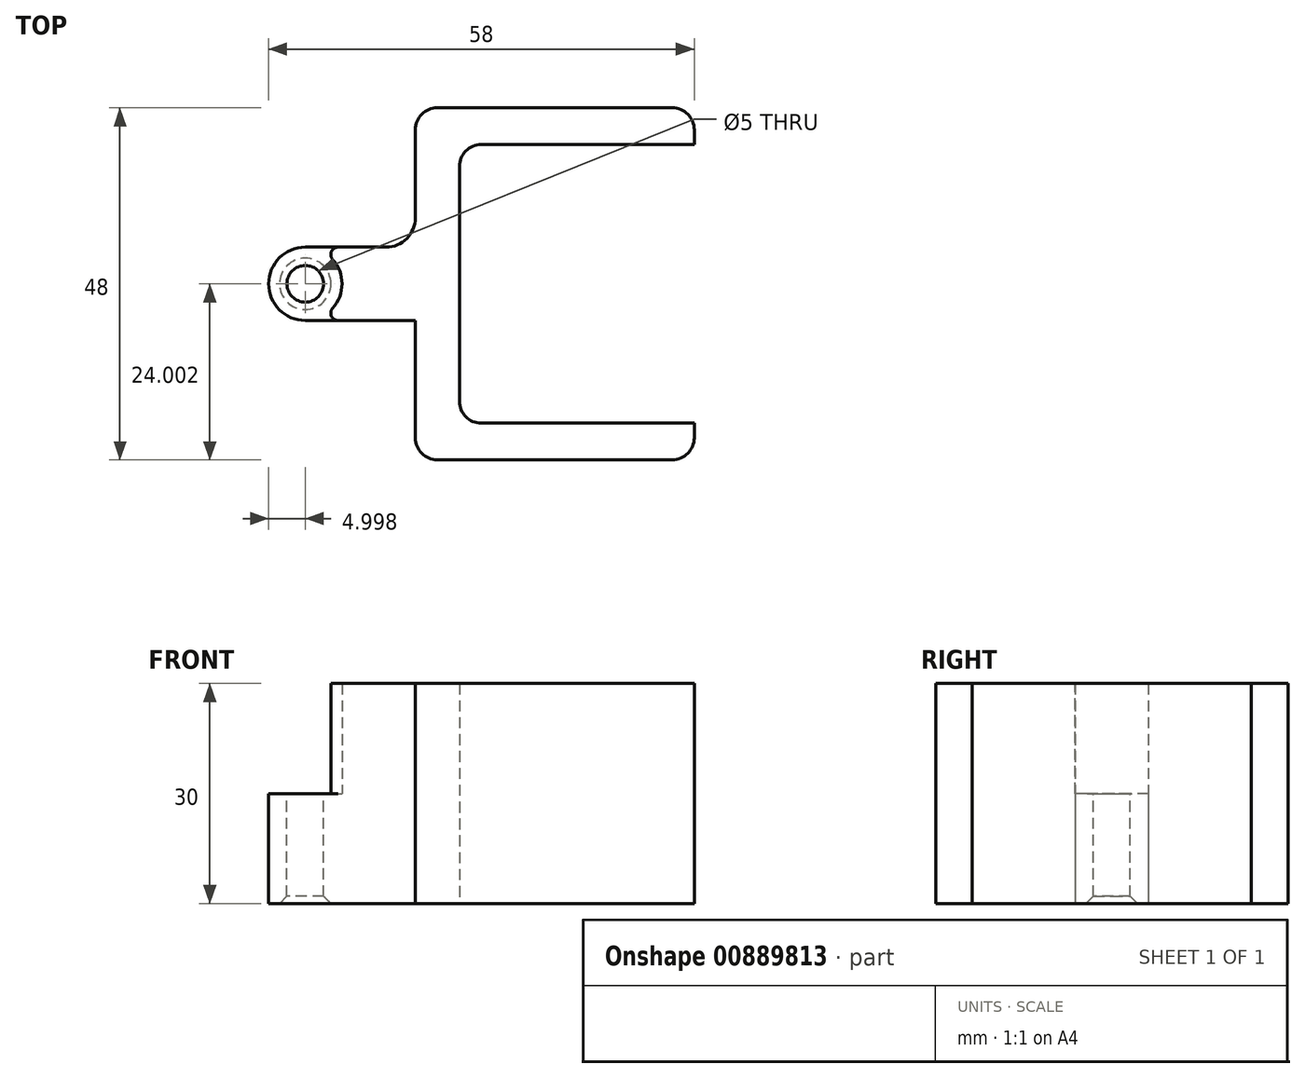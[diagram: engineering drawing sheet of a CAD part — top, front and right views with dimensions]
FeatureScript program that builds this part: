
annotation { "Feature Type Name" : "Feature", "Feature Type Description" : "" }
export const myFeature = defineFeature(function(context is Context, id is Id, definition is map)
    precondition{}
    {
        {
            var Q0;
            Q0=qCreatedBy(makeId("Top.planeOp"),FACE);
            var sketch = newSketch(context, id + "F0", { "sketchPlane" : qUnion([Q0])});
            skCircle(sketch, "E0", {"center": v(-71.58, 14.1) * mm, "radius": 5 * mm});
            skLineSegment(sketch, "E1.bottom", {"start": v(-71.58, 19.1) * mm, "end": v(-56.58, 19.1) * mm});
            skLineSegment(sketch, "E1.top", {"start": v(-71.58, 9.1) * mm, "end": v(-56.58, 9.1) * mm});
            skLineSegment(sketch, "E1.left", {"start": v(-71.58, 19.1) * mm, "end": v(-71.58, 9.1) * mm});
            skLineSegment(sketch, "E1.right", {"start": v(-56.58, 19.1) * mm, "end": v(-56.58, 9.1) * mm});
            skLineSegment(sketch, "E2.bottom", {"start": v(-56.58, 33.1) * mm, "end": v(-50.58, 33.1) * mm});
            skLineSegment(sketch, "E2.top", {"start": v(-56.58, -4.9) * mm, "end": v(-50.58, -4.9) * mm});
            skLineSegment(sketch, "E2.left", {"start": v(-56.58, 33.1) * mm, "end": v(-56.58, -4.9) * mm});
            skLineSegment(sketch, "E2.right", {"start": v(-50.58, 33.1) * mm, "end": v(-50.58, -4.9) * mm});
            skLineSegment(sketch, "E3.bottom", {"start": v(-56.58, 33.1) * mm, "end": v(-18.58, 33.1) * mm});
            skLineSegment(sketch, "E3.top", {"start": v(-56.58, 38.1) * mm, "end": v(-18.58, 38.1) * mm});
            skLineSegment(sketch, "E3.left", {"start": v(-56.58, 33.1) * mm, "end": v(-56.58, 38.1) * mm});
            skLineSegment(sketch, "E3.right", {"start": v(-18.58, 33.1) * mm, "end": v(-18.58, 38.1) * mm});
            skLineSegment(sketch, "E4.bottom", {"start": v(-56.58, -4.9) * mm, "end": v(-18.58, -4.9) * mm});
            skLineSegment(sketch, "E4.top", {"start": v(-56.58, -9.9) * mm, "end": v(-18.58, -9.9) * mm});
            skLineSegment(sketch, "E4.left", {"start": v(-56.58, -4.9) * mm, "end": v(-56.58, -9.9) * mm});
            skLineSegment(sketch, "E4.right", {"start": v(-18.58, -4.9) * mm, "end": v(-18.58, -9.9) * mm});
            skSolve(sketch);
        }
        {
            var Q0;
            {var subQ1=sQuery(id+"F0.wireOp",EDGE,"E1.bottom");Q0=makeQuery(id+"F0.imprint","IMPRINT",FACE,{"disambiguationData":[TD([[makeQuery(id+"F0.imprint","IMPRINT",EDGE,{"derivedFrom":subQ1}),-1.0]])]});}
            extrude(context, id + "F1", {"entities" : qUnion([Q0]), "depth" : 30 * mm, "offsetDistance" : 25 * mm});
        }
        {
            var Q0;
            Q0=makeQuery(id+"F0.imprint","IMPRINT",FACE,{"disambiguationData":[TD([[makeQuery(id+"F0.imprint","IMPRINT",EDGE,{"derivedFrom":sQuery(id+"F0.wireOp",EDGE,"E3.top")}),-1.0]])]});
            var Q1;
            {var subQ0=sQuery(id+"F0.wireOp",EDGE,"E2.right");Q1=makeQuery(id+"F0.imprint","IMPRINT",FACE,{"disambiguationData":[TD([[makeQuery(id+"F0.imprint","IMPRINT",EDGE,{"derivedFrom":subQ0}),-1.0]])]});}
            var Q2;
            Q2=makeQuery(id+"F0.imprint","IMPRINT",FACE,{"disambiguationData":[TD([[makeQuery(id+"F0.imprint","IMPRINT",EDGE,{"derivedFrom":sQuery(id+"F0.wireOp",EDGE,"E4.top")}),1.0]])]});
            extrude(context, id + "F2", {"entities" : qUnion([Q0, Q1, Q2]), "operationType" : NewBodyOperationType.ADD, "depth" : 30 * mm, "offsetDistance" : 25 * mm});
        }
        {
            var Q0;
            {var subQ0=sQuery(id+"F0.wireOp",EDGE,"E1.left");Q0=makeQuery(id+"F0.imprint","IMPRINT",FACE,{"disambiguationData":[TD([[makeQuery(id+"F0.imprint","IMPRINT",EDGE,{"derivedFrom":subQ0}),1.0]])]});}
            var Q1;
            {var subQ0=sQuery(id+"F0.wireOp",EDGE,"E1.left");Q1=makeQuery(id+"F0.imprint","IMPRINT",FACE,{"disambiguationData":[TD([[makeQuery(id+"F0.imprint","IMPRINT",EDGE,{"derivedFrom":subQ0}),-1.0]])]});}
            extrude(context, id + "F3", {"entities" : qUnion([Q0, Q1]), "operationType" : NewBodyOperationType.ADD, "depth" : 15 * mm, "offsetDistance" : 25 * mm});
        }
        {
            var Q0;
            Q0=makeQuery(id+"F3.opExtrude","CAP_FACE",FACE,{"disambiguationData":[OSD([sQuery(id+"F0.wireOp",EDGE,"E0")])],"isStart":false});
            var sketch = newSketch(context, id + "F4", { "sketchPlane" : qUnion([Q0])});
            skCircle(sketch, "E5", {"center": v(-71.58, 14.1) * mm, "radius": 2.5 * mm});
            skSolve(sketch);
        }
        {
            var Q0;
            Q0=makeQuery(id+"F4.imprint","IMPRINT",FACE,{"disambiguationData":[TD([[makeQuery(id+"F4.imprint","IMPRINT",EDGE,{"derivedFrom":sQuery(id+"F4.wireOp",EDGE,"E5")}),1.0]])]});
            extrude(context, id + "F5", {"entities" : qUnion([Q0]), "operationType" : NewBodyOperationType.REMOVE, "oppositeDirection" : true, "depth" : 25 * mm, "offsetDistance" : 25 * mm});
        }
        {
            var Q0;
            Q0=makeQuery(id+"F2.opExtrude","SWEPT_EDGE",EDGE,{"disambiguationData":[OSD([sQuery(id+"F0.wireOp",EDGE,"E4.top"),sQuery(id+"F0.wireOp",EDGE,"E4.right")])]});
            var Q1;
            Q1=makeQuery(id+"F2.opExtrude","SWEPT_EDGE",EDGE,{"disambiguationData":[OSD([sQuery(id+"F0.wireOp",EDGE,"E3.top"),sQuery(id+"F0.wireOp",EDGE,"E3.right")])]});
            var Q2;
            Q2=makeQuery(id+"F2.opExtrude","SWEPT_EDGE",EDGE,{"disambiguationData":[OSD([sQuery(id+"F0.wireOp",EDGE,"E2.right"),sQuery(id+"F0.wireOp",EDGE,"E3.bottom")])]});
            var Q3;
            Q3=makeQuery(id+"F2.opExtrude","SWEPT_EDGE",EDGE,{"disambiguationData":[OSD([sQuery(id+"F0.wireOp",EDGE,"E2.right"),sQuery(id+"F0.wireOp",EDGE,"E4.bottom")])]});
            var Q4;
            Q4=makeQuery(id+"F2.opExtrude","SWEPT_EDGE",EDGE,{"disambiguationData":[OSD([sQuery(id+"F0.wireOp",EDGE,"E4.top"),sQuery(id+"F0.wireOp",EDGE,"E4.left")])]});
            var Q5;
            Q5=makeQuery(id+"F2.opExtrude","SWEPT_EDGE",EDGE,{"disambiguationData":[OSD([sQuery(id+"F0.wireOp",EDGE,"E3.top"),sQuery(id+"F0.wireOp",EDGE,"E3.left")])]});
            fillet(context, id + "F6", {"entities" : qUnion([Q0, Q1, Q2, Q3, Q4, Q5]), "radius" : 3 * mm, "tangentPropagation" : true, "allowEdgeOverflow" : false});
        }
        {
            var Q0;
            Q0=makeQuery(id+"F1.opExtrude","SWEPT_EDGE",EDGE,{"disambiguationData":[OSD([sQuery(id+"F0.wireOp",EDGE,"E1.top"),sQuery(id+"F0.wireOp",EDGE,"E2.left")])]});
            var Q1;
            Q1=makeQuery(id+"F1.opExtrude","SWEPT_EDGE",EDGE,{"disambiguationData":[OSD([sQuery(id+"F0.wireOp",EDGE,"E1.bottom"),sQuery(id+"F0.wireOp",EDGE,"E2.left")])]});
            fillet(context, id + "F7", {"entities" : qUnion([Q0, Q1]), "radius" : 4 * mm, "tangentPropagation" : true, "allowEdgeOverflow" : false});
        }
        {
            var Q0;
            {var subQ0=sQuery(id+"F0.wireOp",EDGE,"E0");var subQ1=sQuery(id+"F0.wireOp",EDGE,"E1.bottom");Q0=makeQuery(id+"F3.boolean.opBoolean","SPLIT",EDGE,{"disambiguationData":[topologyDisambiguationEdgeConnected([makeQuery(id+"F1.opExtrude","SWEPT_FACE",FACE,{"disambiguationData":[OSD([subQ0])]})])],"derivedFrom":makeQuery(id+"F1.opExtrude","SWEPT_EDGE",EDGE,{"disambiguationData":[OSD([subQ0,subQ1,sQuery(id+"F0.wireOp",EDGE,"E1.left")])]})});}
            var Q1;
            {var subQ0=sQuery(id+"F0.wireOp",EDGE,"E0");var subQ1=sQuery(id+"F0.wireOp",EDGE,"E1.top");Q1=makeQuery(id+"F3.boolean.opBoolean","SPLIT",EDGE,{"disambiguationData":[topologyDisambiguationEdgeConnected([makeQuery(id+"F1.opExtrude","SWEPT_FACE",FACE,{"disambiguationData":[OSD([subQ0])]})])],"derivedFrom":makeQuery(id+"F1.opExtrude","SWEPT_EDGE",EDGE,{"disambiguationData":[OSD([subQ0,subQ1,sQuery(id+"F0.wireOp",EDGE,"E1.left")])]})});}
            fillet(context, id + "F8", {"entities" : qUnion([Q0, Q1]), "radius" : 1 * mm, "tangentPropagation" : true, "allowEdgeOverflow" : false});
        }
        {
            var Q0;
            {var subQ0=sQuery(id+"F0.wireOp",EDGE,"E0");var subQ1=sQuery(id+"F0.wireOp",EDGE,"E2.left");Q0=makeQuery(id+"F5.boolean.opBoolean","INTERSECT",EDGE,{"derivedFrom":[makeQuery(id+"F3.boolean.opBoolean","MERGE",FACE,{"derivedFrom":[makeQuery(id+"F2.boolean.opBoolean","MERGE",FACE,{"derivedFrom":[makeQuery(id+"F1.opExtrude","CAP_FACE",FACE,{"disambiguationData":[OSD([subQ0,sQuery(id+"F0.wireOp",EDGE,"E1.bottom"),sQuery(id+"F0.wireOp",EDGE,"E1.top"),subQ1])],"isStart":true}),makeQuery(id+"F2.opExtrude","CAP_FACE",FACE,{"disambiguationData":[OSD([subQ1,sQuery(id+"F0.wireOp",EDGE,"E2.right"),sQuery(id+"F0.wireOp",EDGE,"E3.bottom"),sQuery(id+"F0.wireOp",EDGE,"E3.top"),sQuery(id+"F0.wireOp",EDGE,"E3.left"),sQuery(id+"F0.wireOp",EDGE,"E3.right"),sQuery(id+"F0.wireOp",EDGE,"E4.bottom"),sQuery(id+"F0.wireOp",EDGE,"E4.top"),sQuery(id+"F0.wireOp",EDGE,"E4.left"),sQuery(id+"F0.wireOp",EDGE,"E4.right")])],"isStart":true})]}),makeQuery(id+"F3.opExtrude","CAP_FACE",FACE,{"disambiguationData":[OSD([subQ0])],"isStart":true})]}),makeQuery(id+"F5.opExtrude","SWEPT_FACE",FACE,{"disambiguationData":[OSD([sQuery(id+"F4.wireOp",EDGE,"E5")])]})]});}
            chamfer(context, id + "F9", {"entities" : qUnion([Q0]), "width" : 1 * mm, "tangentPropagation" : true});
        }
    });
